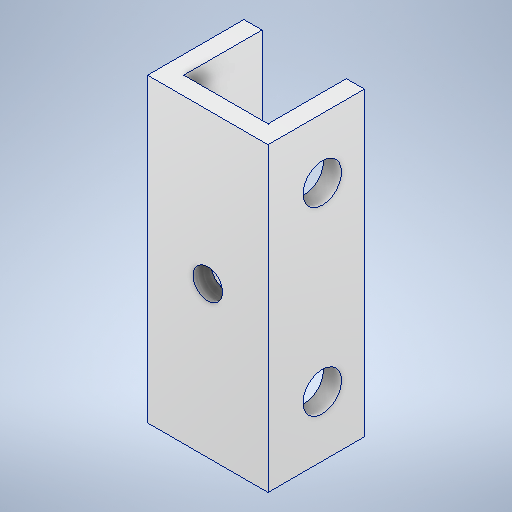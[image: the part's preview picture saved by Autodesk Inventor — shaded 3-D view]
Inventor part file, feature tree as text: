
AUTODESK INVENTOR PART (.ipt)
format: ipt  version: 2025 (Build 290162000, 162)  size: 276,992 bytes
history: native  units: mm
features: sketch x3, hole x2, other x1, extrude x1
ambient origin geometry x8: Origin, YZ Plane, XZ Plane, XY Plane, X Axis, Y Axis, Z Axis, Center Point
bodies: Body1 (feature_tree)
feature tree (7):
  other  "Těleso1"
  extrude  "Vysunutí1"  Depth=8.0mm
  hole  "Díra1"  [1 undecoded]
  hole  "Díra2"  [1 undecoded]
  sketch  "Náčrt1"
  sketch  "Náčrt2"
  sketch  "Náčrt3"
note: 2 required parameter values undecoded (feature->parameter linkage not recoverable at this tier; creation-order binding heuristic only, values carry confidence <= 0.55)
